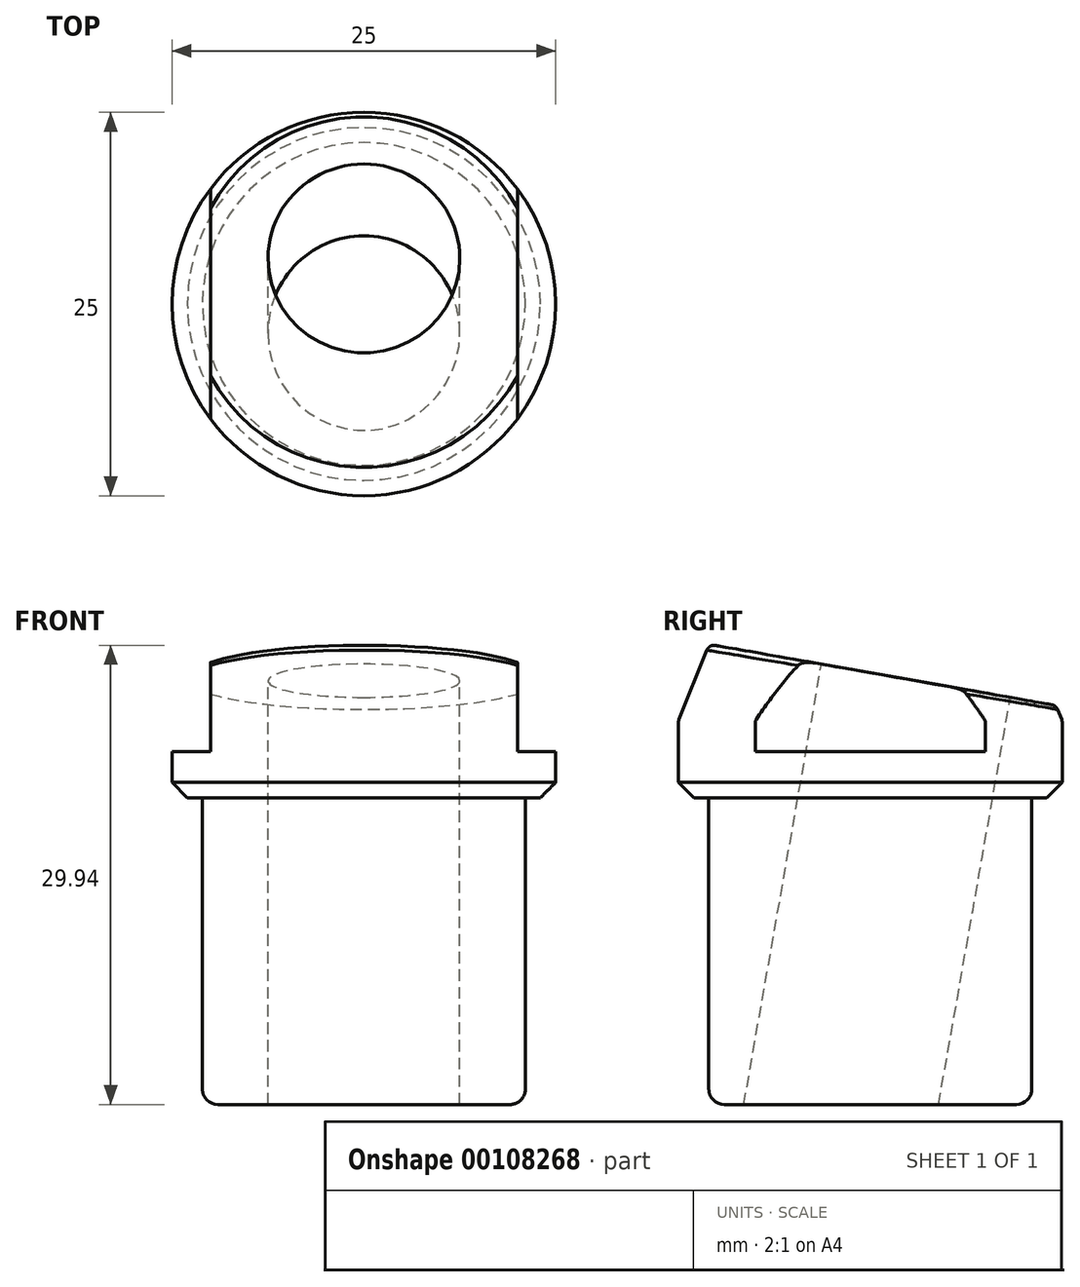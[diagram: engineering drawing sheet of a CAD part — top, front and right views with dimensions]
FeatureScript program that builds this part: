
annotation { "Feature Type Name" : "Feature", "Feature Type Description" : "" }
export const myFeature = defineFeature(function(context is Context, id is Id, definition is map)
    precondition{}
    {
        {
            var Q0;
            Q0=qCreatedBy(makeId("Top.planeOp"),FACE);
            var sketch = newSketch(context, id + "F0", { "sketchPlane" : qUnion([Q0])});
            skCircle(sketch, "E0", {"center": v(0, 0) * mm, "radius": 10.53 * mm});
            skSolve(sketch);
        }
        {
            var Q0;
            Q0=qSketchRegion(id+"F0",true);
            extrude(context, id + "F1", {"entities" : qUnion([Q0]), "oppositeDirection" : true, "depth" : 20 * mm});
        }
        {
            var Q0;
            Q0=makeQuery(id+"F1.opExtrude","CAP_FACE",FACE,{"disambiguationData":[OSD([sQuery(id+"F0.wireOp",EDGE,"E0")])],"isStart":true});
            var sketch = newSketch(context, id + "F2", { "sketchPlane" : qUnion([Q0])});
            skSolve(sketch);
        }
        {
            var Q0;
            Q0=makeQuery(id+"F2.imprint","IMPRINT",FACE,{"disambiguationData":[TD([[makeQuery(id+"F2.imprint","IMPRINT",EDGE,{"derivedFrom":makeQuery(id+"F1.opExtrude","CAP_EDGE",EDGE,{"disambiguationData":[OSD([sQuery(id+"F0.wireOp",EDGE,"E0")])],"isStart":true})}),1.0]])]});
            var sketch = newSketch(context, id + "F3", { "sketchPlane" : qUnion([Q0])});
            skCircle(sketch, "E1", {"center": v(0, 0) * mm, "radius": 12.5 * mm});
            skSolve(sketch);
        }
        {
            var Q0;
            Q0=qSketchRegion(id+"F3",true);
            extrude(context, id + "F4", {"entities" : qUnion([Q0]), "operationType" : NewBodyOperationType.ADD, "depth" : 10 * mm});
        }
        {
            var Q0;
            Q0=makeQuery(id+"F4.opExtrude","CAP_EDGE",EDGE,{"disambiguationData":[OSD([sQuery(id+"F3.wireOp",EDGE,"E1")])],"isStart":false});
            chamfer(context, id + "F5", {"entities" : qUnion([Q0]), "chamferType" : ChamferType.TWO_OFFSETS, "width1" : 2 * mm, "oppositeDirection" : false, "width2" : 5 * mm, "tangentPropagation" : true});
        }
        {
            var Q0;
            Q0=qCreatedBy(makeId("Top.planeOp"),FACE);
            cPlane(context, id + "F6", {"entities" : qUnion([Q0]), "cplaneType" : CPlaneType.OFFSET, "offset" : 5 * mm, "width" : 150 * mm, "height" : 150 * mm});
        }
        {
            var Q0;
            Q0=qCreatedBy(id+"F6.planeOp",FACE);
            var sketch = newSketch(context, id + "F7", { "sketchPlane" : qUnion([Q0])});
            skLineSegment(sketch, "E2", {"start": v(-31.05, -12.5) * mm, "end": v(31.83, -12.5) * mm});
            skCircle(sketch, "E3.0", {"center": v(0, 0) * mm, "radius": 12.5 * mm});
            skSolve(sketch);
        }
        {
            var Q0;
            Q0=makeQuery(id+"F4.opExtrude","CAP_EDGE",EDGE,{"disambiguationData":[OSD([sQuery(id+"F3.wireOp",EDGE,"E1")])],"isStart":true});
            chamfer(context, id + "F8", {"entities" : qUnion([Q0]), "width" : 1 * mm, "tangentPropagation" : true});
        }
        {
            var Q0;
            {var subQ0=sQuery(id+"F3.wireOp",EDGE,"E1");Q0=makeQuery(id+"F5.opChamfer","BLEND_EDGE",EDGE,{"blendedFrom":[makeQuery(id+"F4.opExtrude","CAP_EDGE",EDGE,{"disambiguationData":[OSD([subQ0])],"isStart":false}),makeQuery(id+"F4.opExtrude","SWEPT_FACE",FACE,{"disambiguationData":[OSD([subQ0])]})],"blendedInto":[makeQuery(id+"F4.opExtrude","SWEPT_FACE",FACE,{"disambiguationData":[OSD([subQ0])]})]});}
            fillet(context, id + "F9", {"entities" : qUnion([Q0]), "radius" : 0.5 * mm, "tangentPropagation" : true, "allowEdgeOverflow" : false});
        }
        {
            var Q0;
            Q0=qCreatedBy(makeId("Right.planeOp"),FACE);
            var sketch = newSketch(context, id + "F10", { "sketchPlane" : qUnion([Q0])});
            skLineSegment(sketch, "E4.0", {"start": v(9.53, -20) * mm, "end": v(-9.53, -20) * mm, "construction": true});
            skLineSegment(sketch, "E5", {"start": v(16.9, 5.17) * mm, "end": v(-15.87, 10.95) * mm});
            skLineSegment(sketch, "E6", {"start": v(9.87, 6.4) * mm, "end": v(5.71, -17.14) * mm});
            skLineSegment(sketch, "E7", {"start": v(-3.92, 8.84) * mm, "end": v(-8.12, -15) * mm});
            skLineSegment(sketch, "E8", {"start": v(9.87, 6.4) * mm, "end": v(12.5, 21.4) * mm});
            skLineSegment(sketch, "E9", {"start": v(-1.44, -17.38) * mm, "end": v(7.2, 31.55) * mm, "construction": true});
            skLineSegment(sketch, "E10.0", {"start": v(-10.5, 10) * mm, "end": v(10.5, 10) * mm, "construction": true});
            skSolve(sketch);
        }
        {
            var Q0;
            Q0=sQuery(id+"F10.wireOp",EDGE,"E5");
            var Q1;
            Q1=qCreatedBy(makeId("Top.planeOp"),FACE);
            cPlane(context, id + "F11", {"entities" : qUnion([Q0, Q1]), "cplaneType" : CPlaneType.LINE_ANGLE, "offset" : 25 * mm, "angle" : 0 * degree, "width" : 150 * mm, "height" : 150 * mm});
        }
        {
            var Q0;
            Q0=qCreatedBy(id+"F11.planeOp",FACE);
            var sketch = newSketch(context, id + "F12", { "sketchPlane" : qUnion([Q0])});
            skPoint(sketch, "E11.0", {"position": v(0, -1.6) * mm});
            skCircle(sketch, "E12", {"center": v(0, -1.6) * mm, "radius": 6.25 * mm});
            skSolve(sketch);
        }
        {
            var Q0;
            Q0 = qSketchRegion(id + "F12", true);
            extrude(context, id + "F13", {"entities" : qUnion([Q0]), "operationType" : NewBodyOperationType.REMOVE, "endBound" : BoundingType.THROUGH_ALL, "depth" : 25 * mm, "hasSecondDirection" : true, "secondDirectionBound" : SecondDirectionBoundingType.THROUGH_ALL, "secondDirectionOppositeDirection" : true, "secondDirectionDepth" : 25 * mm});
        }
        {
            var Q0;
            Q0=qCreatedBy(id+"F11.planeOp",FACE);
            var sketch = newSketch(context, id + "F14", { "sketchPlane" : qUnion([Q0])});
            skLineSegment(sketch, "E13.bottom", {"start": v(18.2, 18.36) * mm, "end": v(-17.42, 18.36) * mm});
            skLineSegment(sketch, "E13.top", {"start": v(18.2, -15.38) * mm, "end": v(-17.42, -15.38) * mm});
            skLineSegment(sketch, "E13.left", {"start": v(18.2, 18.36) * mm, "end": v(18.2, -15.38) * mm});
            skLineSegment(sketch, "E13.right", {"start": v(-17.42, 18.36) * mm, "end": v(-17.42, -15.38) * mm});
            skSolve(sketch);
        }
        {
            var Q0;
            Q0 = qSketchRegion(id + "F14", true);
            extrude(context, id + "F15", {"entities" : qUnion([Q0]), "operationType" : NewBodyOperationType.REMOVE, "endBound" : BoundingType.THROUGH_ALL, "oppositeDirection" : true, "depth" : 25 * mm});
        }
        {
            var Q0;
            Q0=makeQuery(id+"F15.boolean.opBoolean","INTERSECT",EDGE,{"derivedFrom":[makeQuery(id+"F5.opChamfer","BLEND_FACE",FACE,{"disambiguationData":[OSD([sQuery(id+"F3.wireOp",EDGE,"E1")])]}),makeQuery(id+"F15.opExtrude","CAP_FACE",FACE,{"disambiguationData":[OSD([sQuery(id+"F14.wireOp",EDGE,"E13.bottom"),sQuery(id+"F14.wireOp",EDGE,"E13.top"),sQuery(id+"F14.wireOp",EDGE,"E13.left"),sQuery(id+"F14.wireOp",EDGE,"E13.right")])],"isStart":true})]});
            fillet(context, id + "F16", {"entities" : qUnion([Q0]), "radius" : 0.5 * mm, "tangentPropagation" : true, "allowEdgeOverflow" : false});
        }
        {
            var Q0;
            Q0=makeQuery(id+"F4.opExtrude","CAP_FACE",FACE,{"disambiguationData":[OSD([sQuery(id+"F3.wireOp",EDGE,"E1")])],"isStart":true});
            cPlane(context, id + "F17", {"entities" : qUnion([Q0]), "cplaneType" : CPlaneType.OFFSET, "offset" : 3 * mm, "oppositeDirection" : true, "width" : 150 * mm, "height" : 150 * mm});
        }
        {
            var Q0;
            Q0=qCreatedBy(id+"F17.planeOp",FACE);
            var sketch = newSketch(context, id + "F18", { "sketchPlane" : qUnion([Q0])});
            skLineSegment(sketch, "E14.bottom", {"start": v(10, -26.25) * mm, "end": v(52.1, -26.25) * mm});
            skLineSegment(sketch, "E14.top", {"start": v(10, 26.25) * mm, "end": v(52.1, 26.25) * mm});
            skLineSegment(sketch, "E14.left", {"start": v(10, -26.25) * mm, "end": v(10, 26.25) * mm});
            skLineSegment(sketch, "E14.right", {"start": v(52.1, -26.25) * mm, "end": v(52.1, 26.25) * mm});
            skPoint(sketch, "E14.middle", {"position": v(31.05, 0) * mm});
            skLineSegment(sketch, "E15.bottom", {"start": v(-10, -27.91) * mm, "end": v(-31.53, -27.91) * mm});
            skLineSegment(sketch, "E15.top", {"start": v(-10, 27.91) * mm, "end": v(-31.53, 27.91) * mm});
            skLineSegment(sketch, "E15.left", {"start": v(-10, -27.91) * mm, "end": v(-10, 27.91) * mm});
            skLineSegment(sketch, "E15.right", {"start": v(-31.53, -27.91) * mm, "end": v(-31.53, 27.91) * mm});
            skPoint(sketch, "E15.middle", {"position": v(-20.77, 0) * mm});
            skSolve(sketch);
        }
        {
            var Q0;
            Q0 = qSketchRegion(id + "F18", true);
            extrude(context, id + "F19", {"entities" : qUnion([Q0]), "operationType" : NewBodyOperationType.REMOVE, "endBound" : BoundingType.THROUGH_ALL, "oppositeDirection" : true, "depth" : 25 * mm});
        }
        {
            var Q0;
            Q0=makeQuery(id+"F1.opExtrude","CAP_EDGE",EDGE,{"disambiguationData":[OSD([sQuery(id+"F0.wireOp",EDGE,"E0")])],"isStart":false});
            fillet(context, id + "F20", {"entities" : qUnion([Q0]), "radius" : 1 * mm, "tangentPropagation" : true, "allowEdgeOverflow" : false});
        }
    });
